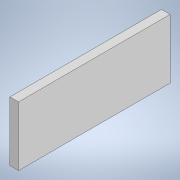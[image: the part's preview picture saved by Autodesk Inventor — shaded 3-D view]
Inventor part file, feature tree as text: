
AUTODESK INVENTOR PART (.ipt)
format: ipt  version: 2020 (Build 240168000, 168)  size: 87,552 bytes
history: native  units: mm
features: other x1, extrude x1, sketch x1
ambient origin geometry x8: Origin, YZ Plane, XZ Plane, XY Plane, X Axis, Y Axis, Z Axis, Center Point
bodies: Body1 (feature_tree)
feature tree (3):
  other  "Bryła1"
  extrude  "Wyciągnięcie proste1"  Depth=140.0mm
  sketch  "Szkic1"
